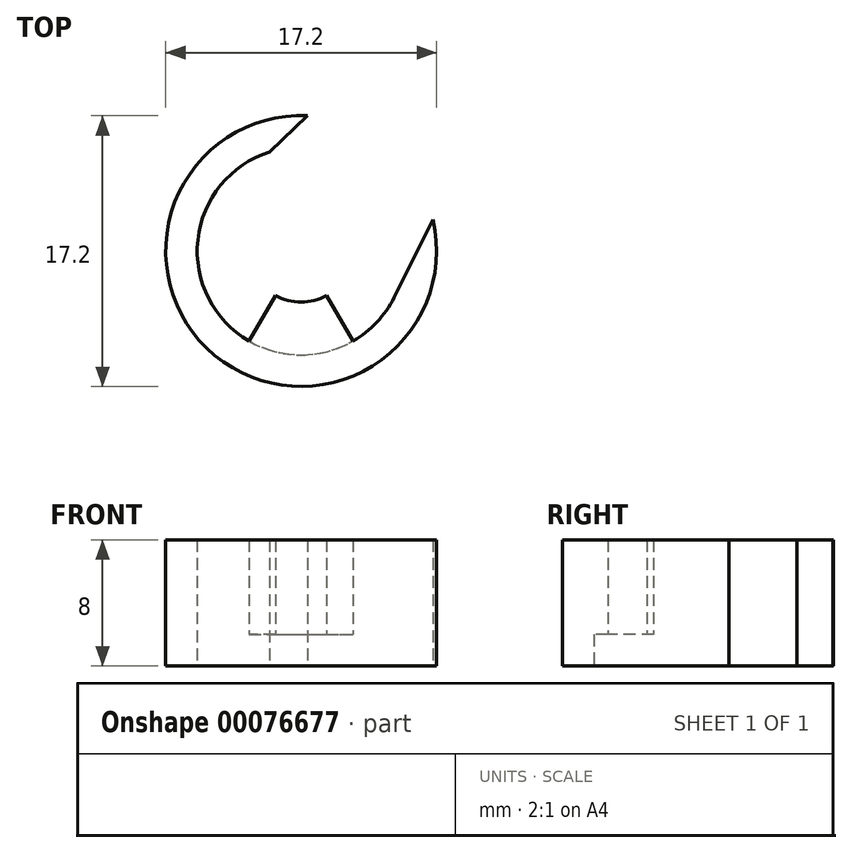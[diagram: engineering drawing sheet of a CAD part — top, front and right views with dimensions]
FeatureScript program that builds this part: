
annotation { "Feature Type Name" : "Feature", "Feature Type Description" : "" }
export const myFeature = defineFeature(function(context is Context, id is Id, definition is map)
    precondition{}
    {
        {
            var Q0;
            Q0=qCreatedBy(makeId("Top.planeOp"),FACE);
            var sketch = newSketch(context, id + "F0", { "sketchPlane" : qUnion([Q0])});
            skCircle(sketch, "E0", {"center": v(0, 0) * mm, "radius": 6.6 * mm});
            skCircle(sketch, "E1", {"center": v(0, 0) * mm, "radius": 8.6 * mm});
            skArc(sketch, "E2", {"start": v(-1.62, -2.81) * mm, "mid": v(0, -3.25) * mm, "end": v(1.62, -2.81) * mm});
            skLineSegment(sketch, "E3", {"start": v(1.63, -2.81) * mm, "end": v(3.3, -5.72) * mm});
            skLineSegment(sketch, "E4", {"start": v(-1.62, -2.81) * mm, "end": v(-3.3, -5.72) * mm});
            skLineSegment(sketch, "E5", {"start": v(-2, 6.29) * mm, "end": v(0.4, 8.6) * mm});
            skLineSegment(sketch, "E6", {"start": v(5.9, -2.95) * mm, "end": v(8.37, 1.99) * mm});
            skSolve(sketch);
        }
        {
            var Q0;
            {var subQ0=sQuery(id+"F0.wireOp",EDGE,"E5");Q0=makeQuery(id+"F0.imprint","IMPRINT",FACE,{"disambiguationData":[TD([[makeQuery(id+"F0.imprint","IMPRINT",EDGE,{"derivedFrom":subQ0}),1.0]])]});}
            extrude(context, id + "F1", {"entities" : qUnion([Q0]), "depth" : 8 * mm});
        }
        {
            var Q0;
            Q0=makeQuery(id+"F0.imprint","IMPRINT",FACE,{"disambiguationData":[TD([[makeQuery(id+"F0.imprint","IMPRINT",EDGE,{"derivedFrom":sQuery(id+"F0.wireOp",EDGE,"E2")}),-1.0]])]});
            extrude(context, id + "F2", {"entities" : qUnion([Q0]), "operationType" : NewBodyOperationType.ADD, "depth" : 8 * mm, "hasSecondDirection" : true, "secondDirectionOppositeDirection" : false, "secondDirectionDepth" : 2 * mm});
        }
    });
